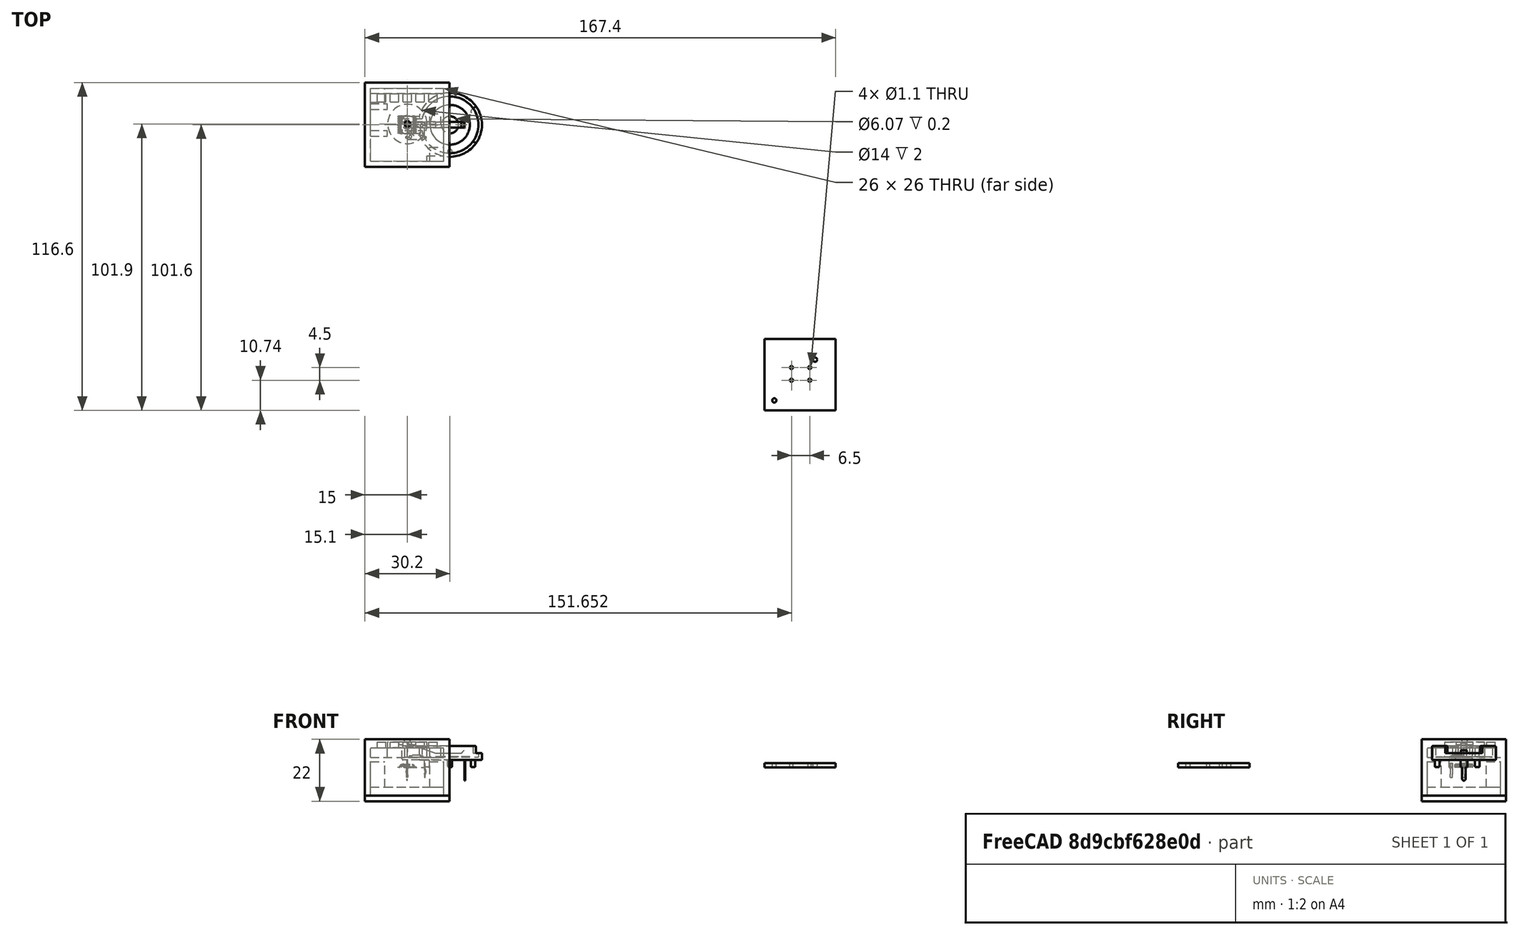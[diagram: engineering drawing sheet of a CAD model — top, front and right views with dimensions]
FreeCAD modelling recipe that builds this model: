
FCSTD DOCUMENT  (FreeCAD 0.17R13541 (Git))
Label: BoxSup
License: All rights reserved
LicenseURL: http://en.wikipedia.org/wiki/All_rights_reserved
objects: Part::Feature×30, App::Part×30, Part::Box×16, Part::MultiFuse×5, Part::Cut×4, Part::Cylinder×3
note: 58 computed .brp shape members not serialized (recipe doc carries the construction recipe); baked Part::Feature solids carry a one-line shape summary decoded from their .brp

FEATURE [Part::Box] Box  label="MainInside"
  AttacherType = Attacher::AttachEngine3D
  Height = 17
  Length = 26
  Placement = pos=(-13,-13,-10) rot=(0,0,1;0rad)
  Width = 26
FEATURE [Part::Box] Box001  label="MainOutside"
  AttacherType = Attacher::AttachEngine3D
  Height = 20
  Length = 30
  Placement = pos=(-15,-15,-10) rot=(0,0,1;0rad)
  Width = 30
FEATURE [Part::Feature] Part__Feature  label="SOLID"
  shape: bbox 2 x 1.25 x 1.1 mm, 50 faces (baked)
FEATURE [App::Part] LED_0805_2012Metric
  Group = -> [Part__Feature]
  License = CC BY 3.0
  LicenseURL = http://creativecommons.org/licenses/by/3.0/
  Origin = -> Origin
  Placement = pos=(144.272,-79.248,1.65) rot=(0,0,-1;1.5708rad)
FEATURE [Part::Feature] Part__Feature001  label="SOLID001"
  shape: bbox 7.174 x 6 x 7.8 mm, 105 faces (baked)
FEATURE [App::Part] SW_PUSH_6mm
  Group = -> [Part__Feature001]
  License = CC BY 3.0
  LicenseURL = http://creativecommons.org/licenses/by/3.0/
  Origin = -> Origin001
  Placement = pos=(136.652,-86.36,1.65) rot=(0,0,1;0rad)
FEATURE [Part::Feature] Part__Feature002  label="SOLID002"
  shape: bbox 1.6 x 0.8 x 0.45 mm, 26 faces (baked)
FEATURE [App::Part] R_0603_1608Metric
  Group = -> [Part__Feature002]
  License = CC BY 3.0
  LicenseURL = http://creativecommons.org/licenses/by/3.0/
  Origin = -> Origin002
  Placement = pos=(147.701,-98.679,1.65) rot=(0,0,1;0rad)
FEATURE [Part::Feature] Part__Feature003  label="SOLID003"
  shape: bbox 1.6 x 0.8 x 0.45 mm, 26 faces (baked)
FEATURE [App::Part] R_0603_1608Metric001
  Group = -> [Part__Feature003]
  License = CC BY 3.0
  LicenseURL = http://creativecommons.org/licenses/by/3.0/
  Origin = -> Origin003
  Placement = pos=(145.411,-99.187,1.65) rot=(0,0,1;1.5708rad)
FEATURE [Part::Feature] Part__Feature004  label="SOLID004"
  shape: bbox 6.4 x 6.5 x 1.2 mm, 336 faces (baked)
FEATURE [App::Part] TSSOP_20_4_4x6_5mm_P0_65mm
  Group = -> [Part__Feature004]
  License = CC BY 3.0
  LicenseURL = http://creativecommons.org/licenses/by/3.0/
  Origin = -> Origin004
  Placement = pos=(148.336,-93.81,1.65) rot=(0,0,1;1.5708rad)
FEATURE [Part::Feature] Part__Feature005  label="SOLID005"
  shape: bbox 2 x 1.25 x 1.1 mm, 50 faces (baked)
FEATURE [App::Part] LED_0805_2012Metric001
  Group = -> [Part__Feature005]
  License = CC BY 3.0
  LicenseURL = http://creativecommons.org/licenses/by/3.0/
  Origin = -> Origin005
  Placement = pos=(130.556,-79.248,1.65) rot=(0,0,-1;1.5708rad)
FEATURE [Part::Feature] Part__Feature006  label="SOLID006"
  shape: bbox 2 x 1.25 x 1.1 mm, 50 faces (baked)
FEATURE [App::Part] LED_0805_2012Metric002
  Group = -> [Part__Feature006]
  License = CC BY 3.0
  LicenseURL = http://creativecommons.org/licenses/by/3.0/
  Origin = -> Origin006
  Placement = pos=(135.128,-79.248,1.65) rot=(0,0,-1;1.5708rad)
FEATURE [Part::Feature] Part__Feature007  label="SOLID007"
  shape: bbox 2 x 1.25 x 1.1 mm, 50 faces (baked)
FEATURE [App::Part] LED_0805_2012Metric003
  Group = -> [Part__Feature007]
  License = CC BY 3.0
  LicenseURL = http://creativecommons.org/licenses/by/3.0/
  Origin = -> Origin007
  Placement = pos=(139.7,-79.248,1.65) rot=(0,0,-1;1.5708rad)
FEATURE [Part::Feature] Part__Feature008  label="SOLID008"
  shape: bbox 2 x 1.25 x 1.1 mm, 50 faces (baked)
FEATURE [App::Part] LED_0805_2012Metric004
  Group = -> [Part__Feature008]
  License = CC BY 3.0
  LicenseURL = http://creativecommons.org/licenses/by/3.0/
  Origin = -> Origin008
  Placement = pos=(148.844,-79.248,1.65) rot=(0,0,-1;1.5708rad)
FEATURE [Part::Feature] Part__Feature009  label="SOLID009"
  shape: bbox 1.6 x 0.8 x 0.45 mm, 26 faces (baked)
FEATURE [App::Part] R_0603_1608Metric002
  Group = -> [Part__Feature009]
  License = CC BY 3.0
  LicenseURL = http://creativecommons.org/licenses/by/3.0/
  Origin = -> Origin009
  Placement = pos=(132.588,-79.248,1.65) rot=(0,0,-1;1.5708rad)
FEATURE [Part::Feature] Part__Feature010  label="SOLID010"
  shape: bbox 1.6 x 0.8 x 0.45 mm, 26 faces (baked)
FEATURE [App::Part] R_0603_1608Metric003
  Group = -> [Part__Feature010]
  License = CC BY 3.0
  LicenseURL = http://creativecommons.org/licenses/by/3.0/
  Origin = -> Origin010
  Placement = pos=(137.16,-79.248,1.65) rot=(0,0,-1;1.5708rad)
FEATURE [Part::Feature] Part__Feature011  label="SOLID011"
  shape: bbox 1.6 x 0.8 x 0.45 mm, 26 faces (baked)
FEATURE [App::Part] R_0603_1608Metric004
  Group = -> [Part__Feature011]
  License = CC BY 3.0
  LicenseURL = http://creativecommons.org/licenses/by/3.0/
  Origin = -> Origin011
  Placement = pos=(141.732,-79.248,1.65) rot=(0,0,-1;1.5708rad)
FEATURE [Part::Feature] Part__Feature012  label="SOLID012"
  shape: bbox 1.6 x 0.8 x 0.45 mm, 26 faces (baked)
FEATURE [App::Part] R_0603_1608Metric005
  Group = -> [Part__Feature012]
  License = CC BY 3.0
  LicenseURL = http://creativecommons.org/licenses/by/3.0/
  Origin = -> Origin012
  Placement = pos=(146.304,-79.248,1.65) rot=(0,0,-1;1.5708rad)
FEATURE [Part::Feature] Part__Feature013  label="SOLID013"
  shape: bbox 1.6 x 0.8 x 0.45 mm, 26 faces (baked)
FEATURE [App::Part] R_0603_1608Metric006
  Group = -> [Part__Feature013]
  License = CC BY 3.0
  LicenseURL = http://creativecommons.org/licenses/by/3.0/
  Origin = -> Origin013
  Placement = pos=(150.876,-79.248,1.65) rot=(0,0,-1;1.5708rad)
FEATURE [Part::Feature] Part__Feature014  label="SOLID014"
  shape: bbox 1.6 x 0.8 x 0.8 mm, 28 faces (baked)
FEATURE [App::Part] C_0603_1608Metric
  Group = -> [Part__Feature014]
  License = CC BY 3.0
  LicenseURL = http://creativecommons.org/licenses/by/3.0/
  Origin = -> Origin014
  Placement = pos=(142.494,-94.488,1.65) rot=(0,0,-1;1.5708rad)
FEATURE [Part::Feature] Part__Feature015  label="SOLID015"
  shape: bbox 1.6 x 0.8 x 0.8 mm, 28 faces (baked)
FEATURE [App::Part] C_0603_1608Metric001
  Group = -> [Part__Feature015]
  License = CC BY 3.0
  LicenseURL = http://creativecommons.org/licenses/by/3.0/
  Origin = -> Origin015
  Placement = pos=(143.891,-94.488,1.65) rot=(0,0,-1;1.5708rad)
FEATURE [Part::Feature] Part__Feature016  label="SOLID016"
  shape: bbox 1.6 x 0.8 x 0.8 mm, 28 faces (baked)
FEATURE [App::Part] C_0603_1608Metric002
  Group = -> [Part__Feature016]
  License = CC BY 3.0
  LicenseURL = http://creativecommons.org/licenses/by/3.0/
  Origin = -> Origin016
  Placement = pos=(129.286,-95.631,1.65) rot=(0,0,1;0.785398rad)
FEATURE [Part::Feature] Part__Feature017  label="SOLID017"
  shape: bbox 1.6 x 0.8 x 0.8 mm, 28 faces (baked)
FEATURE [App::Part] C_0603_1608Metric003
  Group = -> [Part__Feature017]
  License = CC BY 3.0
  LicenseURL = http://creativecommons.org/licenses/by/3.0/
  Origin = -> Origin017
  Placement = pos=(128.778,-94.107,1.65) rot=(0,0,1;0.785398rad)
FEATURE [Part::Feature] Part__Feature018  label="SOLID018"
  shape: bbox 29.3 x 24.64 x 13.25 mm, 71 faces (baked)
FEATURE [App::Part] BatteryHolder_Keystone_103_1x20mm
  Group = -> [Part__Feature018]
  License = CC BY 3.0
  LicenseURL = http://creativecommons.org/licenses/by/3.0/
  Origin = -> Origin018
  Placement = pos=(130.556,-98.044,-0.05) rot=(0.92388,0.382683,0;3.14159rad)
FEATURE [Part::Feature] Part__Feature019  label="SOLID019"
  shape: bbox 2.5 x 3 x 1.2 mm, 76 faces (baked)
FEATURE [App::Part] SOT_23
  Group = -> [Part__Feature019]
  License = CC BY 3.0
  LicenseURL = http://creativecommons.org/licenses/by/3.0/
  Origin = -> Origin019
  Placement = pos=(130.81,-88.646,1.65) rot=(0,0,1;0rad)
FEATURE [Part::Feature] Part__Feature020  label="SOLID020"
  shape: bbox 2.5 x 3 x 1.2 mm, 76 faces (baked)
FEATURE [App::Part] SOT_23001
  Group = -> [Part__Feature020]
  License = CC BY 3.0
  LicenseURL = http://creativecommons.org/licenses/by/3.0/
  Origin = -> Origin020
  Placement = pos=(129.286,-85.09,1.65) rot=(0,0,1;3.14159rad)
FEATURE [Part::Feature] Part__Feature021  label="SOLID021"
  shape: bbox 1.6 x 0.8 x 0.45 mm, 26 faces (baked)
FEATURE [App::Part] R_0603_1608Metric007
  Group = -> [Part__Feature021]
  License = CC BY 3.0
  LicenseURL = http://creativecommons.org/licenses/by/3.0/
  Origin = -> Origin021
  Placement = pos=(128.27,-88.8745,1.65) rot=(0,0,1;1.5708rad)
FEATURE [Part::Feature] Part__Feature022  label="SOLID022"
  shape: bbox 1.6 x 0.8 x 0.45 mm, 26 faces (baked)
FEATURE [App::Part] R_0603_1608Metric008
  Group = -> [Part__Feature022]
  License = CC BY 3.0
  LicenseURL = http://creativecommons.org/licenses/by/3.0/
  Origin = -> Origin022
  Placement = pos=(131.699,-85.217,1.65) rot=(0,0,1;1.5708rad)
FEATURE [Part::Feature] Part__Feature023  label="SOLID023"
  shape: bbox 2.5 x 3 x 1.2 mm, 76 faces (baked)
FEATURE [App::Part] SOT_23002
  Group = -> [Part__Feature023]
  License = CC BY 3.0
  LicenseURL = http://creativecommons.org/licenses/by/3.0/
  Origin = -> Origin023
  Placement = pos=(135.89,-97.79,1.65) rot=(0,0,1;1.5708rad)
FEATURE [Part::Feature] Part__Feature024  label="SOLID024"
  shape: bbox 2.5 x 3 x 1.2 mm, 76 faces (baked)
FEATURE [App::Part] SOT_23003
  Group = -> [Part__Feature024]
  License = CC BY 3.0
  LicenseURL = http://creativecommons.org/licenses/by/3.0/
  Origin = -> Origin024
  Placement = pos=(139.446,-97.79,1.65) rot=(0,0,1;1.5708rad)
FEATURE [Part::Feature] Part__Feature025  label="SOLID025"
  shape: bbox 2.5 x 3 x 1.2 mm, 76 faces (baked)
FEATURE [App::Part] SOT_23004
  Group = -> [Part__Feature025]
  License = CC BY 3.0
  LicenseURL = http://creativecommons.org/licenses/by/3.0/
  Origin = -> Origin025
  Placement = pos=(143.002,-97.79,1.65) rot=(0,0,1;0rad)
FEATURE [Part::Feature] Part__Feature026  label="SOLID026"
  shape: bbox 1.6 x 0.8 x 0.45 mm, 26 faces (baked)
FEATURE [App::Part] R_0603_1608Metric009
  Group = -> [Part__Feature026]
  License = CC BY 3.0
  LicenseURL = http://creativecommons.org/licenses/by/3.0/
  Origin = -> Origin026
  Placement = pos=(135.89,-100.33,1.65) rot=(0,0,1;3.14159rad)
FEATURE [Part::Feature] Part__Feature027  label="SOLID027"
  shape: bbox 1.6 x 0.8 x 0.45 mm, 26 faces (baked)
FEATURE [App::Part] R_0603_1608Metric010
  Group = -> [Part__Feature027]
  License = CC BY 3.0
  LicenseURL = http://creativecommons.org/licenses/by/3.0/
  Origin = -> Origin027
  Placement = pos=(133.35,-99.5425,1.65) rot=(0,0,-1;1.5708rad)
FEATURE [Part::Feature] Part__Feature028  label="SOLID028"
  shape: bbox 1.6 x 0.8 x 0.45 mm, 26 faces (baked)
FEATURE [App::Part] R_0603_1608Metric011
  Group = -> [Part__Feature028]
  License = CC BY 3.0
  LicenseURL = http://creativecommons.org/licenses/by/3.0/
  Origin = -> Origin028
  Placement = pos=(139.192,-100.33,1.65) rot=(0,0,1;0rad)
FEATURE [Part::Feature] Part__Feature029  label="COMPOUND"
  shape: bbox 25.4 x 25.4 x 1.6 mm, 12 faces (baked)
FEATURE [App::Part] Open_CASCADE_STEP_translator_6_9_1
  Group = -> [LED_0805_2012Metric,SW_PUSH_6mm,R_0603_1608Metric,R_0603_1608Metric001,TSSOP_20_4_4x6_5mm_P0_65mm,LED_0805_2012Metric001,LED_0805_2012Metric002,LED_0805_2012Metric003,LED_0805_2012Metric004,R_0603_1608Metric002,R_0603_1608Metric003,R_0603_1608Metric004,R_0603_1608Metric005,R_0603_1608Metric006,C_0603_1608Metric,C_0603_1608Metric001,C_0603_1608Metric002,C_0603_1608Metric003,+12 more]
  License = CC BY 3.0
  LicenseURL = http://creativecommons.org/licenses/by/3.0/
  Origin = -> Origin029
  Placement = pos=(-139.7,88.9,2) rot=(0,0,1;0rad)
FEATURE [Part::Cut] Cut
  Base = -> Box001
  Tool = -> Box
FEATURE [Part::Box] Box002  label="L1"
  AttacherType = Attacher::AttachEngine3D
  Height = 2
  Length = 3
  Placement = pos=(-10.61,8.11,7) rot=(0,0,1;0rad)
  Width = 3
FEATURE [Part::Box] Box003  label="L2"
  AttacherType = Attacher::AttachEngine3D
  Height = 2
  Length = 3
  Placement = pos=(-6.04,8.11,7) rot=(0,0,1;0rad)
  Width = 3
FEATURE [Part::Box] Box004  label="L3"
  AttacherType = Attacher::AttachEngine3D
  Height = 2
  Length = 3
  Placement = pos=(-1.47,8.11,7) rot=(0,0,1;0rad)
  Width = 3
FEATURE [Part::Box] Box005  label="L4"
  AttacherType = Attacher::AttachEngine3D
  Height = 2
  Length = 3
  Placement = pos=(3.1,8.11,7) rot=(0,0,1;0rad)
  Width = 3
FEATURE [Part::Box] Box006  label="L5"
  AttacherType = Attacher::AttachEngine3D
  Height = 2
  Length = 3
  Placement = pos=(7.67,8.11,7) rot=(0,0,1;0rad)
  Width = 3
FEATURE [Part::Cylinder] Cylinder  label="But"
  Angle = 360
  AttacherType = Attacher::AttachEngine3D
  Height = 2
  Placement = pos=(0.1,0.3,7) rot=(0,0,1;0rad)
  Radius = 7
FEATURE [Part::Cylinder] Cylinder001  label="ButTouch"
  Angle = 360
  AttacherType = Attacher::AttachEngine3D
  Height = 2
  Placement = pos=(0.1,0.3,8) rot=(0,0,1;0rad)
  Radius = 3
FEATURE [Part::Cut] Cut001
  Base = -> Cut
  Tool = -> Cylinder
FEATURE [Part::MultiFuse] Fusion
  Shapes = -> [Box002,Box006,Box005,Box003,Box004]
FEATURE [Part::Cut] Cut002
  Base = -> Cut001
  Tool = -> Fusion
FEATURE [Part::MultiFuse] Fusion001
  Shapes = -> [Cylinder001,Cut002]
FEATURE [Part::Box] Box007  label="CubeDestek"
  AttacherType = Attacher::AttachEngine3D
  Height = 3.4
  Length = 26
  Placement = pos=(-13,11.2,3.6) rot=(0,0,1;0rad)
  Width = 1.8
FEATURE [Part::Box] Box008  label="CubeDestek2"
  AttacherType = Attacher::AttachEngine3D
  Height = 3.4
  Length = 4
  Placement = pos=(8,0,3.6) rot=(0,0,1;0rad)
  Width = 4
FEATURE [Part::Box] Box009  label="CubeDestek3"
  AttacherType = Attacher::AttachEngine3D
  Height = 3.4
  Length = 6
  Placement = pos=(-13,-4,3.6) rot=(0,0,1;0rad)
  Width = 2
FEATURE [Part::Box] Box010  label="CubeDestek4"
  AttacherType = Attacher::AttachEngine3D
  Height = 3.4
  Length = 6
  Placement = pos=(-13,5.5,3.6) rot=(0,0,1;0rad)
  Width = 2
FEATURE [Part::Box] Box011  label="CubeDestek5"
  AttacherType = Attacher::AttachEngine3D
  Height = 3.4
  Length = 6
  Placement = pos=(7,-13,3.6) rot=(0,0,1;0rad)
  Width = 2
FEATURE [Part::MultiFuse] Fusion002  label="FusionDestek"
  Shapes = -> [Box011,Box010,Box008,Box007,Box009]
FEATURE [Part::Box] Box012  label="KapakGenis"
  AttacherType = Attacher::AttachEngine3D
  Height = 2
  Length = 30
  Placement = pos=(-15,-15,-12) rot=(0,0,1;0rad)
  Width = 30
FEATURE [Part::Box] Box013  label="KapakIc"
  AttacherType = Attacher::AttachEngine3D
  Height = 3
  Length = 26
  Placement = pos=(-13,-13,-10) rot=(0,0,1;0rad)
  Width = 26
FEATURE [Part::Box] Box014  label="KapakCikinti1"
  AttacherType = Attacher::AttachEngine3D
  Height = 9
  Length = 5
  Placement = pos=(-13,8,-7) rot=(0,0,1;0rad)
  Width = 5
FEATURE [Part::Box] Box015  label="KapakCikinti2"
  AttacherType = Attacher::AttachEngine3D
  Height = 9
  Length = 5
  Placement = pos=(8,-13,-7) rot=(0,0,1;0rad)
  Width = 5
FEATURE [Part::Cylinder] Cylinder002  label="ButTouch001"
  Angle = 360
  AttacherType = Attacher::AttachEngine3D
  Height = 1
  Placement = pos=(0.1,0.3,9) rot=(0,0,1;0rad)
  Radius = 1
FEATURE [Part::Cut] Cut003
  Base = -> Fusion001
  Tool = -> Cylinder002
FEATURE [Part::MultiFuse] Fusion003
  Shapes = -> [Fusion002,Cut003]
FEATURE [Part::MultiFuse] Fusion004
  Shapes = -> [Box015,Box013,Box014,Box012]
